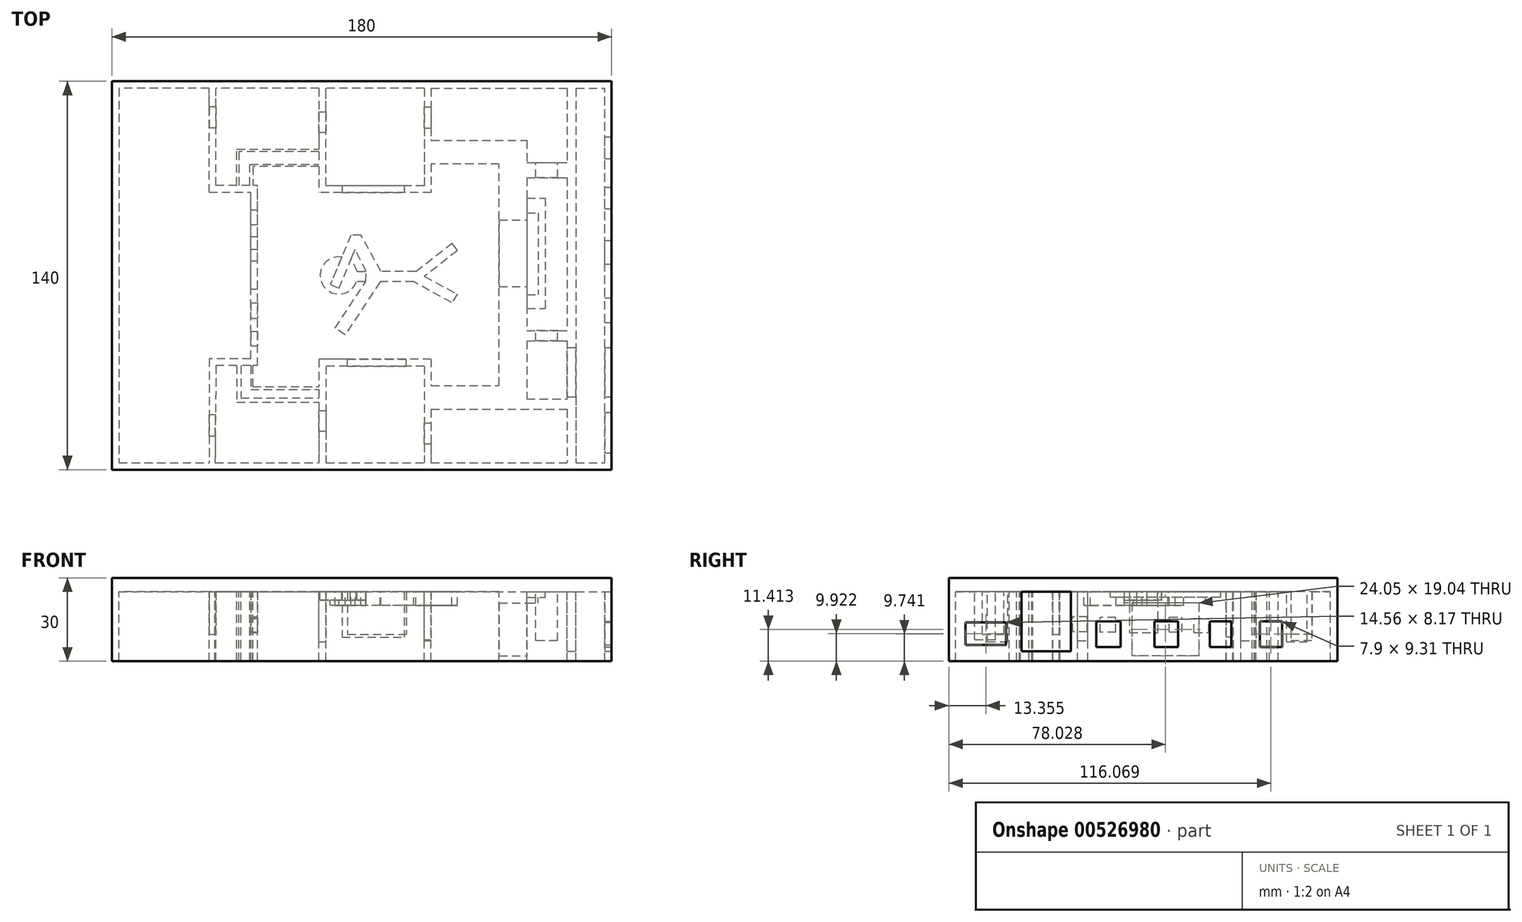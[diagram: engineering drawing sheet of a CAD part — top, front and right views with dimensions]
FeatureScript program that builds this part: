
annotation { "Feature Type Name" : "Feature", "Feature Type Description" : "" }
export const myFeature = defineFeature(function(context is Context, id is Id, definition is map)
    precondition{}
    {
        {
            var Q0;
            Q0=qCreatedBy(makeId("Top.planeOp"),FACE);
            var sketch = newSketch(context, id + "F0", { "sketchPlane" : qUnion([Q0])});
            skLineSegment(sketch, "E0", {"start": v(0, 0) * mm, "end": v(0, 140) * mm});
            skLineSegment(sketch, "E1", {"start": v(0, 140) * mm, "end": v(180, 140) * mm});
            skLineSegment(sketch, "E2", {"start": v(180, 140) * mm, "end": v(180, 0) * mm});
            skLineSegment(sketch, "E3", {"start": v(180, 0) * mm, "end": v(0, 0) * mm});
            skLineSegment(sketch, "E4", {"start": v(0, 140) * mm, "end": v(0, 136) * mm, "construction": true});
            skLineSegment(sketch, "E5", {"start": v(0, 140) * mm, "end": v(4, 140) * mm, "construction": true});
            skLineSegment(sketch, "E6", {"start": v(4, 136) * mm, "end": v(4, 0) * mm});
            skLineSegment(sketch, "E7", {"start": v(4, 136) * mm, "end": v(180, 136) * mm});
            skLineSegment(sketch, "E8", {"start": v(65.64, 100) * mm, "end": v(125.64, 100) * mm});
            skLineSegment(sketch, "E9", {"start": v(125.64, 100) * mm, "end": v(125.64, 40) * mm});
            skLineSegment(sketch, "E10", {"start": v(125.64, 40) * mm, "end": v(65.64, 40) * mm});
            skLineSegment(sketch, "E11", {"start": v(65.64, 100) * mm, "end": v(65.64, 40) * mm});
            skCircle(sketch, "E12", {"center": v(81.7, 70) * mm, "radius": 6.72 * mm});
            skPoint(sketch, "E12.centerSnap0", {"position": v(65.64, 70) * mm});
            skLineSegment(sketch, "E13", {"start": v(81.75, 65.36) * mm, "end": v(78.62, 66.66) * mm});
            skLineSegment(sketch, "E14", {"start": v(109.48, 71.46) * mm, "end": v(122.4, 81.58) * mm});
            skLineSegment(sketch, "E15", {"start": v(122.4, 81.58) * mm, "end": v(124.45, 78.96) * mm});
            skLineSegment(sketch, "E16", {"start": v(124.45, 78.96) * mm, "end": v(112.55, 69.63) * mm});
            skLineSegment(sketch, "E17", {"start": v(112.55, 69.63) * mm, "end": v(124.43, 63.28) * mm});
            skLineSegment(sketch, "E18", {"start": v(124.43, 63.28) * mm, "end": v(122.4, 60.22) * mm});
            skLineSegment(sketch, "E19", {"start": v(122.4, 60.22) * mm, "end": v(108.68, 67.74) * mm});
            skLineSegment(sketch, "E20", {"start": v(108.68, 67.74) * mm, "end": v(96.6, 67.74) * mm});
            skLineSegment(sketch, "E21", {"start": v(96.6, 67.74) * mm, "end": v(84, 48.65) * mm});
            skLineSegment(sketch, "E22", {"start": v(84, 48.65) * mm, "end": v(80.38, 51.04) * mm});
            skLineSegment(sketch, "E23", {"start": v(80.38, 51.04) * mm, "end": v(91.4, 67.74) * mm});
            skLineSegment(sketch, "E24", {"start": v(91.4, 67.74) * mm, "end": v(88.04, 67.74) * mm});
            skLineSegment(sketch, "E25", {"start": v(109.48, 71.46) * mm, "end": v(96.88, 71.46) * mm});
            skLineSegment(sketch, "E26", {"start": v(88.27, 71.46) * mm, "end": v(91.57, 71.46) * mm});
            skLineSegment(sketch, "E27", {"start": v(91.57, 71.46) * mm, "end": v(87.62, 79.42) * mm});
            skLineSegment(sketch, "E28", {"start": v(96.88, 71.46) * mm, "end": v(89.7, 84.59) * mm});
            skLineSegment(sketch, "E29", {"start": v(89.7, 84.59) * mm, "end": v(86.1, 84.59) * mm});
            skLineSegment(sketch, "E30", {"start": v(86.1, 84.59) * mm, "end": v(78.62, 66.66) * mm});
            skLineSegment(sketch, "E31", {"start": v(81.75, 65.36) * mm, "end": v(87.62, 79.42) * mm});
            skLineSegment(sketch, "E32", {"start": v(91.4, 67.74) * mm, "end": v(91.57, 71.46) * mm});
            skSolve(sketch);
        }
        {
            var Q0;
            Q0=makeQuery(id+"F0.imprint","IMPRINT",FACE,{"disambiguationData":[TD([[makeQuery(id+"F0.imprint","IMPRINT",EDGE,{"derivedFrom":sQuery(id+"F0.wireOp",EDGE,"E0")}),-1.0]])]});
            var Q1;
            {var subQ1=sQuery(id+"F0.wireOp",EDGE,"E6");Q1=makeQuery(id+"F0.imprint","IMPRINT",FACE,{"disambiguationData":[TD([[makeQuery(id+"F0.imprint","IMPRINT",EDGE,{"derivedFrom":subQ1}),1.0]])]});}
            var Q2;
            Q2=makeQuery(id+"F0.imprint","IMPRINT",FACE,{"disambiguationData":[TD([[makeQuery(id+"F0.imprint","IMPRINT",EDGE,{"derivedFrom":sQuery(id+"F0.wireOp",EDGE,"E8")}),-1.0]])]});
            var Q3;
            Q3=makeQuery(id+"F0.imprint","IMPRINT",FACE,{"disambiguationData":[TD([[makeQuery(id+"F0.imprint","IMPRINT",EDGE,{"derivedFrom":sQuery(id+"F0.wireOp",EDGE,"E14")}),-1.0]])]});
            var Q4;
            {var subQ0=sQuery(id+"F0.wireOp",EDGE,"E13");Q4=makeQuery(id+"F0.imprint","IMPRINT",FACE,{"disambiguationData":[TD([[makeQuery(id+"F0.imprint","IMPRINT",EDGE,{"derivedFrom":subQ0}),1.0]])]});}
            var Q5;
            {var subQ5=sQuery(id+"F0.wireOp",EDGE,"E13");Q5=makeQuery(id+"F0.imprint","IMPRINT",FACE,{"disambiguationData":[TD([[makeQuery(id+"F0.imprint","IMPRINT",EDGE,{"derivedFrom":subQ5}),-1.0]])]});}
            var Q6;
            {var subQ0=sQuery(id+"F0.wireOp",EDGE,"E26");Q6=makeQuery(id+"F0.imprint","IMPRINT",FACE,{"disambiguationData":[TD([[makeQuery(id+"F0.imprint","IMPRINT",EDGE,{"derivedFrom":subQ0}),1.0]])]});}
            var Q7;
            {var subQ0=sQuery(id+"F0.wireOp",EDGE,"E24");Q7=makeQuery(id+"F0.imprint","IMPRINT",FACE,{"disambiguationData":[TD([[makeQuery(id+"F0.imprint","IMPRINT",EDGE,{"derivedFrom":subQ0}),-1.0]])]});}
            extrude(context, id + "F1", {"entities" : qUnion([Q0, Q1, Q2, Q3, Q4, Q5, Q6, Q7]), "depth" : 5 * mm, "offsetDistance" : 25 * mm});
        }
        {
            var Q0;
            {var subQ0=sQuery(id+"F0.wireOp",EDGE,"E13");Q0=makeQuery(id+"F0.imprint","IMPRINT",FACE,{"disambiguationData":[TD([[makeQuery(id+"F0.imprint","IMPRINT",EDGE,{"derivedFrom":subQ0}),1.0]])]});}
            extrude(context, id + "F2", {"entities" : qUnion([Q0]), "oppositeDirection" : true, "depth" : 3 * mm, "offsetDistance" : 25 * mm});
        }
        {
            var Q0;
            Q0=makeQuery(id+"F0.imprint","IMPRINT",FACE,{"disambiguationData":[TD([[makeQuery(id+"F0.imprint","IMPRINT",EDGE,{"derivedFrom":sQuery(id+"F0.wireOp",EDGE,"E14")}),-1.0]])]});
            var Q1;
            {var subQ5=sQuery(id+"F0.wireOp",EDGE,"E13");Q1=makeQuery(id+"F0.imprint","IMPRINT",FACE,{"disambiguationData":[TD([[makeQuery(id+"F0.imprint","IMPRINT",EDGE,{"derivedFrom":subQ5}),-1.0]])]});}
            extrude(context, id + "F3", {"entities" : qUnion([Q0, Q1]), "oppositeDirection" : true, "depth" : 5 * mm, "offsetDistance" : 25 * mm});
        }
        {
            var Q0;
            {var subQ0=sQuery(id+"F0.wireOp",EDGE,"E24");Q0=makeQuery(id+"F0.imprint","IMPRINT",FACE,{"disambiguationData":[TD([[makeQuery(id+"F0.imprint","IMPRINT",EDGE,{"derivedFrom":subQ0}),-1.0]])]});}
            extrude(context, id + "F4", {"entities" : qUnion([Q0]), "operationType" : NewBodyOperationType.ADD, "oppositeDirection" : true, "depth" : 3 * mm, "offsetDistance" : 25 * mm});
        }
        {
            var Q0;
            {var subQ0=sQuery(id+"F0.wireOp",EDGE,"E0");var subQ1=sQuery(id+"F0.wireOp",EDGE,"E3");var subQ2=sQuery(id+"F0.wireOp",EDGE,"E1");var subQ3=sQuery(id+"F0.wireOp",EDGE,"E2");Q0=makeQuery(id+"F4.boolean.opBoolean","SPLIT",FACE,{"disambiguationData":[TD([makeQuery(id+"F1.opExtrude","SWEPT_FACE",FACE,{"disambiguationData":[OSD([subQ0])]})])],"derivedFrom":makeQuery(id+"F1.opExtrude","CAP_FACE",FACE,{"disambiguationData":[OSD([subQ0,subQ2,subQ3,subQ1])],"isStart":true})});}
            var sketch = newSketch(context, id + "F5", { "sketchPlane" : qUnion([Q0])});
            skLineSegment(sketch, "E33", {"start": v(0, -140) * mm, "end": v(0, -137.5) * mm, "construction": true});
            skLineSegment(sketch, "E34", {"start": v(0, -140) * mm, "end": v(2.5, -140) * mm, "construction": true});
            skLineSegment(sketch, "E35", {"start": v(180, -140) * mm, "end": v(180, -137.5) * mm, "construction": true});
            skLineSegment(sketch, "E36", {"start": v(180, -140) * mm, "end": v(177.5, -140) * mm, "construction": true});
            skLineSegment(sketch, "E37", {"start": v(180, 0) * mm, "end": v(177.5, 0) * mm, "construction": true});
            skLineSegment(sketch, "E38", {"start": v(180, 0) * mm, "end": v(180, -2.5) * mm, "construction": true});
            skLineSegment(sketch, "E39", {"start": v(177.5, 0) * mm, "end": v(180, 0) * mm});
            skLineSegment(sketch, "E40", {"start": v(180, -140) * mm, "end": v(0, -140) * mm});
            skLineSegment(sketch, "E41", {"start": v(0, 0) * mm, "end": v(180, 0) * mm});
            skLineSegment(sketch, "E42", {"start": v(65.99, -99.84) * mm, "end": v(65.7, -39.85) * mm, "construction": true});
            skLineSegment(sketch, "E43", {"start": v(2.5, -2.5) * mm, "end": v(52.5, -2.5) * mm, "construction": true});
            skLineSegment(sketch, "E44", {"start": v(2.5, -2.5) * mm, "end": v(2.5, -37.5) * mm, "construction": true});
            skLineSegment(sketch, "E45", {"start": v(2.5, -137.5) * mm, "end": v(2.5, -102.5) * mm, "construction": true});
            skLineSegment(sketch, "E46", {"start": v(52.5, -37.5) * mm, "end": v(52.5, -102.5) * mm});
            skLineSegment(sketch, "E47", {"start": v(2.5, -2.5) * mm, "end": v(37.13, -2.5) * mm, "construction": true});
            skLineSegment(sketch, "E48", {"start": v(37.5, -102.5) * mm, "end": v(37.5, -137.5) * mm});
            skLineSegment(sketch, "E49", {"start": v(37.5, -37.5) * mm, "end": v(37.13, -2.5) * mm});
            skLineSegment(sketch, "E50", {"start": v(37.5, -140) * mm, "end": v(35, -140) * mm, "construction": true});
            skLineSegment(sketch, "E51", {"start": v(52.5, -102.5) * mm, "end": v(52.5, -100) * mm, "construction": true});
            skLineSegment(sketch, "E52", {"start": v(35, -100) * mm, "end": v(35, -137.5) * mm});
            skLineSegment(sketch, "E53", {"start": v(52.5, -37.5) * mm, "end": v(50, -37.5) * mm, "construction": true});
            skLineSegment(sketch, "E54", {"start": v(35, -100) * mm, "end": v(50, -100) * mm});
            skLineSegment(sketch, "E55", {"start": v(52.5, -37.5) * mm, "end": v(52.5, -40) * mm, "construction": true});
            skLineSegment(sketch, "E56", {"start": v(37.5, -37.5) * mm, "end": v(35, -37.53) * mm, "construction": true});
            skLineSegment(sketch, "E57", {"start": v(50, -40) * mm, "end": v(35, -40) * mm});
            skLineSegment(sketch, "E58", {"start": v(35, -40) * mm, "end": v(35, -2.5) * mm});
            skLineSegment(sketch, "E59", {"start": v(50, -40) * mm, "end": v(50, -100) * mm});
            skLineSegment(sketch, "E60", {"start": v(112.49, -137.5) * mm, "end": v(114.99, -137.5) * mm, "construction": true});
            skLineSegment(sketch, "E61", {"start": v(114.99, -137.5) * mm, "end": v(114.99, -99.84) * mm});
            skLineSegment(sketch, "E62", {"start": v(114.99, -39.85) * mm, "end": v(114.99, -2.5) * mm});
            skLineSegment(sketch, "E63", {"start": v(74.59, -137.5) * mm, "end": v(77.09, -137.5) * mm, "construction": true});
            skLineSegment(sketch, "E64", {"start": v(114.99, -99.84) * mm, "end": v(114.99, -102.34) * mm, "construction": true});
            skLineSegment(sketch, "E65", {"start": v(112.49, -102.34) * mm, "end": v(77.09, -102.34) * mm});
            skLineSegment(sketch, "E66", {"start": v(77.09, -102.34) * mm, "end": v(77.09, -137.5) * mm});
            skLineSegment(sketch, "E67", {"start": v(112.49, -39.85) * mm, "end": v(112.49, -37.35) * mm, "construction": true});
            skLineSegment(sketch, "E68", {"start": v(112.49, -37.35) * mm, "end": v(77.09, -37.35) * mm});
            skLineSegment(sketch, "E69", {"start": v(112.49, -137.5) * mm, "end": v(77.09, -137.5) * mm});
            skLineSegment(sketch, "E70", {"start": v(74.59, -137.5) * mm, "end": v(37.5, -137.5) * mm});
            skLineSegment(sketch, "E71", {"start": v(35, -137.5) * mm, "end": v(2.5, -137.5) * mm});
            skLineSegment(sketch, "E72", {"start": v(2.5, -137.5) * mm, "end": v(2.5, -2.5) * mm});
            skLineSegment(sketch, "E73", {"start": v(2.5, -2.5) * mm, "end": v(35, -2.5) * mm});
            skLineSegment(sketch, "E74", {"start": v(37.13, -2.5) * mm, "end": v(74.59, -2.5) * mm});
            skLineSegment(sketch, "E75", {"start": v(77.09, -2.5) * mm, "end": v(112.49, -2.5) * mm});
            skLineSegment(sketch, "E76", {"start": v(114.99, -2.5) * mm, "end": v(177.5, -2.5) * mm});
            skLineSegment(sketch, "E77", {"start": v(177.5, -2.5) * mm, "end": v(177.5, -137.5) * mm});
            skLineSegment(sketch, "E78", {"start": v(112.49, -137.5) * mm, "end": v(112.49, -102.34) * mm});
            skLineSegment(sketch, "E79", {"start": v(114.99, -99.84) * mm, "end": v(74.59, -99.84) * mm});
            skLineSegment(sketch, "E80", {"start": v(112.49, -37.35) * mm, "end": v(112.49, -2.5) * mm});
            skLineSegment(sketch, "E81", {"start": v(114.99, -39.85) * mm, "end": v(74.59, -39.85) * mm});
            skLineSegment(sketch, "E82", {"start": v(77.09, -37.35) * mm, "end": v(77.09, -2.5) * mm});
            skLineSegment(sketch, "E83", {"start": v(114.99, -137.5) * mm, "end": v(177.5, -137.5) * mm});
            skLineSegment(sketch, "E84", {"start": v(180, 0) * mm, "end": v(0, 0) * mm});
            skLineSegment(sketch, "E85", {"start": v(0, 0) * mm, "end": v(0, -140) * mm});
            skLineSegment(sketch, "E86", {"start": v(0, -140) * mm, "end": v(180, -140) * mm});
            skLineSegment(sketch, "E87", {"start": v(180, -140) * mm, "end": v(180, 0) * mm});
            skLineSegment(sketch, "E88", {"start": v(49.7, -102.5) * mm, "end": v(49.7, -110.1) * mm});
            skLineSegment(sketch, "E89", {"start": v(49.7, -110.1) * mm, "end": v(74.59, -110.1) * mm});
            skLineSegment(sketch, "E90", {"start": v(74.59, -114.63) * mm, "end": v(45.73, -114.63) * mm});
            skLineSegment(sketch, "E91", {"start": v(45.73, -114.63) * mm, "end": v(45.73, -102.5) * mm});
            skLineSegment(sketch, "E92.bottom", {"start": v(50, -37.5) * mm, "end": v(50, -37.5) * mm});
            skLineSegment(sketch, "E92.top", {"start": v(50, -28.92) * mm, "end": v(50, -28.92) * mm});
            skLineSegment(sketch, "E92.left", {"start": v(50, -37.5) * mm, "end": v(50, -28.92) * mm});
            skLineSegment(sketch, "E92.right", {"start": v(50, -37.5) * mm, "end": v(50, -28.92) * mm});
            skLineSegment(sketch, "E93", {"start": v(50, -28.92) * mm, "end": v(74.59, -28.92) * mm});
            skLineSegment(sketch, "E94", {"start": v(46.44, -37.5) * mm, "end": v(46.44, -25.83) * mm});
            skLineSegment(sketch, "E95", {"start": v(46.44, -25.83) * mm, "end": v(74.59, -25.83) * mm});
            skLineSegment(sketch, "E96", {"start": v(45, -37.5) * mm, "end": v(45, -24.39) * mm});
            skLineSegment(sketch, "E97", {"start": v(45, -24.39) * mm, "end": v(74.59, -24.39) * mm});
            skLineSegment(sketch, "E98", {"start": v(74.59, -109.29) * mm, "end": v(50.75, -109.29) * mm});
            skLineSegment(sketch, "E99", {"start": v(50.75, -109.29) * mm, "end": v(50.75, -102.5) * mm});
            skLineSegment(sketch, "E100", {"start": v(45, -102.5) * mm, "end": v(45, -115.5) * mm});
            skLineSegment(sketch, "E101", {"start": v(45, -115.5) * mm, "end": v(74.59, -115.5) * mm});
            skLineSegment(sketch, "E102", {"start": v(50.68, -37.5) * mm, "end": v(50.68, -29.9) * mm});
            skLineSegment(sketch, "E103", {"start": v(50.68, -29.9) * mm, "end": v(74.59, -29.9) * mm});
            skLineSegment(sketch, "E104", {"start": v(114.99, -118.67) * mm, "end": v(149.45, -118.67) * mm});
            skLineSegment(sketch, "E105", {"start": v(149.45, -118.67) * mm, "end": v(149.45, -21.8) * mm});
            skLineSegment(sketch, "E106", {"start": v(149.45, -21.8) * mm, "end": v(114.99, -21.8) * mm});
            skLineSegment(sketch, "E107", {"start": v(163.9, -137.5) * mm, "end": v(163.9, -2.5) * mm});
            skLineSegment(sketch, "E108", {"start": v(167.19, -137.5) * mm, "end": v(167.19, -2.5) * mm});
            skLineSegment(sketch, "E109", {"start": v(52.5, -102.5) * mm, "end": v(50.75, -102.5) * mm});
            skLineSegment(sketch, "E110", {"start": v(49.7, -102.5) * mm, "end": v(45.73, -102.5) * mm});
            skLineSegment(sketch, "E111", {"start": v(45, -102.5) * mm, "end": v(37.5, -102.5) * mm});
            skLineSegment(sketch, "E112", {"start": v(74.59, -137.5) * mm, "end": v(74.59, -115.5) * mm});
            skLineSegment(sketch, "E113", {"start": v(74.59, -114.63) * mm, "end": v(74.59, -110.1) * mm});
            skLineSegment(sketch, "E114", {"start": v(74.59, -109.29) * mm, "end": v(74.59, -99.84) * mm});
            skLineSegment(sketch, "E115", {"start": v(74.59, -39.85) * mm, "end": v(74.59, -29.9) * mm});
            skLineSegment(sketch, "E116", {"start": v(74.59, -28.92) * mm, "end": v(74.59, -25.83) * mm});
            skLineSegment(sketch, "E117", {"start": v(74.59, -24.39) * mm, "end": v(74.59, -2.5) * mm});
            skLineSegment(sketch, "E118", {"start": v(52.5, -37.5) * mm, "end": v(50.68, -37.5) * mm});
            skLineSegment(sketch, "E119", {"start": v(50, -37.5) * mm, "end": v(46.44, -37.5) * mm});
            skLineSegment(sketch, "E120", {"start": v(45, -37.5) * mm, "end": v(37.5, -37.5) * mm});
            skLineSegment(sketch, "E121", {"start": v(149.45, -110.64) * mm, "end": v(163.9, -110.64) * mm});
            skLineSegment(sketch, "E122", {"start": v(149.45, -105.2) * mm, "end": v(163.9, -105.2) * mm});
            skLineSegment(sketch, "E123", {"start": v(149.45, -21.8) * mm, "end": v(163.9, -21.8) * mm});
            skLineSegment(sketch, "E124", {"start": v(149.45, -25.47) * mm, "end": v(163.9, -25.47) * mm});
            skLineSegment(sketch, "E125", {"start": v(149.45, -46.4) * mm, "end": v(163.9, -46.4) * mm});
            skLineSegment(sketch, "E126", {"start": v(149.45, -50.1) * mm, "end": v(163.9, -50.1) * mm});
            skLineSegment(sketch, "E127", {"start": v(163.9, -110.64) * mm, "end": v(163.9, -105.2) * mm});
            skLineSegment(sketch, "E128", {"start": v(149.45, -110.64) * mm, "end": v(149.45, -105.2) * mm});
            skLineSegment(sketch, "E129", {"start": v(149.45, -50.1) * mm, "end": v(149.45, -46.4) * mm});
            skLineSegment(sketch, "E130", {"start": v(163.9, -50.1) * mm, "end": v(163.9, -46.4) * mm});
            skLineSegment(sketch, "E131", {"start": v(149.45, -25.47) * mm, "end": v(149.45, -21.8) * mm});
            skLineSegment(sketch, "E132", {"start": v(163.9, -25.47) * mm, "end": v(163.9, -21.8) * mm});
            skLineSegment(sketch, "E133", {"start": v(163.9, -46.4) * mm, "end": v(163.9, -50.1) * mm});
            skLineSegment(sketch, "E134", {"start": v(114.99, -30.31) * mm, "end": v(139.5, -30.31) * mm});
            skLineSegment(sketch, "E135", {"start": v(139.5, -30.31) * mm, "end": v(139.5, -110.24) * mm});
            skLineSegment(sketch, "E136", {"start": v(139.5, -110.24) * mm, "end": v(114.99, -110.24) * mm});
            skSolve(sketch);
        }
        {
            var Q0;
            Q0=makeQuery(id+"F5.imprint","IMPRINT",FACE,{"disambiguationData":[TD([[makeQuery(id+"F5.imprint","IMPRINT",EDGE,{"derivedFrom":sQuery(id+"F5.wireOp",EDGE,"E46")}),-1.0]])]});
            var Q1;
            {var subQ0=sQuery(id+"F5.wireOp",EDGE,"E107");Q1=makeQuery(id+"F5.imprint","IMPRINT",FACE,{"disambiguationData":[TD([[makeQuery(id+"F5.imprint","IMPRINT",EDGE,{"derivedFrom":subQ0}),-1.0]])]});}
            var Q2;
            {var subQ1=sQuery(id+"F5.wireOp",EDGE,"zqTt42JP-UiR3-tYYN-FmIC-fksbVnWEhdpc");Q2=makeQuery(id+"F5.imprint","IMPRINT",FACE,{"disambiguationData":[TD([[makeQuery(id+"F5.imprint","IMPRINT",EDGE,{"derivedFrom":subQ1}),-1.0]])]});}
            var Q3;
            {var subQ4=sQuery(id+"F5.wireOp",EDGE,"BBN0Q2NJ-4y6p-QWxy-LSlA-rJ4cVUdJi9dW");Q3=makeQuery(id+"F5.imprint","IMPRINT",FACE,{"disambiguationData":[TD([[makeQuery(id+"F5.imprint","IMPRINT",EDGE,{"derivedFrom":subQ4}),-1.0]])]});}
            var Q4;
            {var subQ1=sQuery(id+"F5.wireOp",EDGE,"E94");Q4=makeQuery(id+"F5.imprint","IMPRINT",FACE,{"disambiguationData":[TD([[makeQuery(id+"F5.imprint","IMPRINT",EDGE,{"derivedFrom":subQ1}),1.0]])]});}
            var Q5;
            {var subQ3=sQuery(id+"F5.wireOp",EDGE,"E88");Q5=makeQuery(id+"F5.imprint","IMPRINT",FACE,{"disambiguationData":[TD([[makeQuery(id+"F5.imprint","IMPRINT",EDGE,{"derivedFrom":subQ3}),1.0]])]});}
            var Q6;
            Q6=sQuery(id+"F5.wireOp",EDGE,"E69");
            var Q7;
            Q7=sQuery(id+"F5.wireOp",EDGE,"E83");
            var Q8;
            Q8=sQuery(id+"F5.wireOp",EDGE,"E61");
            var Q9;
            Q9=sQuery(id+"F5.wireOp",EDGE,"E78");
            var Q10;
            Q10=sQuery(id+"F5.wireOp",EDGE,"E65");
            var Q11;
            Q11=sQuery(id+"F5.wireOp",EDGE,"E79");
            var Q12;
            Q12=sQuery(id+"F5.wireOp",EDGE,"E66");
            var Q13;
            Q13=sQuery(id+"F5.wireOp",EDGE,"xXiJbnCB-tXTr-yrwY-zz4e-hIO52vtba69x");
            var Q14;
            Q14=sQuery(id+"F5.wireOp",EDGE,"E70");
            var Q15;
            Q15=sQuery(id+"F5.wireOp",EDGE,"E48");
            var Q16;
            Q16=sQuery(id+"F5.wireOp",EDGE,"E52");
            var Q17;
            Q17=sQuery(id+"F5.wireOp",EDGE,"E72");
            var Q18;
            Q18=sQuery(id+"F0.wireOp",EDGE,"E6");
            var Q19;
            Q19=sQuery(id+"F5.wireOp",EDGE,"E71");
            var Q20;
            Q20=sQuery(id+"F5.wireOp",EDGE,"Ycx7GNkC-WWnf-lh6J-vGUQ-VtARFQnHF0Q5");
            var Q21;
            Q21=sQuery(id+"F5.wireOp",EDGE,"E54");
            var Q22;
            Q22=sQuery(id+"F5.wireOp",EDGE,"E46");
            var Q23;
            Q23=sQuery(id+"F5.wireOp",EDGE,"E59");
            var Q24;
            Q24=sQuery(id+"F5.wireOp",EDGE,"E57");
            var Q25;
            Q25=sQuery(id+"F5.wireOp",EDGE,"yTd8xMan-KKJn-cybX-pbuV-fECFdfSEL98J");
            var Q26;
            Q26=sQuery(id+"F5.wireOp",EDGE,"E49");
            var Q27;
            Q27=sQuery(id+"F5.wireOp",EDGE,"E58");
            var Q28;
            Q28=sQuery(id+"F5.wireOp",EDGE,"E73");
            var Q29;
            Q29=sQuery(id+"F5.wireOp",EDGE,"E84");
            var Q30;
            Q30=sQuery(id+"F5.wireOp",EDGE,"E74");
            var Q31;
            Q31=sQuery(id+"F5.wireOp",EDGE,"E81");
            var Q32;
            Q32=sQuery(id+"F5.wireOp",EDGE,"E62");
            var Q33;
            Q33=sQuery(id+"F5.wireOp",EDGE,"E80");
            var Q34;
            Q34=sQuery(id+"F5.wireOp",EDGE,"E82");
            var Q35;
            Q35=sQuery(id+"F5.wireOp",EDGE,"S9NegTVv-2bzC-NR3S-rT7V-91NvLfx18yFU");
            var Q36;
            Q36=sQuery(id+"F5.wireOp",EDGE,"E68");
            var Q37;
            Q37=sQuery(id+"F5.wireOp",EDGE,"E76");
            var Q38;
            Q38=sQuery(id+"F5.wireOp",EDGE,"E75");
            var Q39;
            Q39=sQuery(id+"F5.wireOp",EDGE,"E77");
            var Q40;
            Q40=sQuery(id+"F5.wireOp",EDGE,"E87");
            var Q41;
            Q41=sQuery(id+"F5.wireOp",EDGE,"E40");
            extrude(context, id + "F6", {"entities" : qUnion([Q0, Q1, Q2, Q3, Q4, Q5]), "surfaceEntities" : qUnion([Q6, Q7, Q8, Q9, Q10, Q11, Q12, Q13, Q14, Q15, Q16, Q17, Q18, Q19, Q20, Q21, Q22, Q23, Q24, Q25, Q26, Q27, Q28, Q29, Q30, Q31, Q32, Q33, Q34, Q35, Q36, Q37, Q38, Q39, Q40, Q41]), "depth" : 25 * mm, "offsetDistance" : 25 * mm});
        }
        {
            var Q0;
            Q0=makeQuery(id+"F6.opExtrude","SWEPT_FACE",FACE,{"disambiguationData":[OSD([sQuery(id+"F5.wireOp",EDGE,"E46")])]});
            var sketch = newSketch(context, id + "F7", { "sketchPlane" : qUnion([Q0])});
            skLineSegment(sketch, "E137", {"start": v(65.1, 0) * mm, "end": v(65.1, -14.76) * mm});
            skLineSegment(sketch, "E138", {"start": v(65.1, -14.76) * mm, "end": v(75.31, -14.76) * mm});
            skLineSegment(sketch, "E139", {"start": v(75.31, -14.76) * mm, "end": v(75.31, 0) * mm});
            skLineSegment(sketch, "E140", {"start": v(75.31, 0) * mm, "end": v(65.1, 0) * mm});
            skLineSegment(sketch, "E141.bottom", {"start": v(60.18, -14.58) * mm, "end": v(54.57, -14.58) * mm});
            skLineSegment(sketch, "E141.top", {"start": v(60.18, -9.25) * mm, "end": v(54.57, -9.25) * mm});
            skLineSegment(sketch, "E141.left", {"start": v(60.18, -14.58) * mm, "end": v(60.18, -9.25) * mm});
            skLineSegment(sketch, "E141.right", {"start": v(54.57, -14.58) * mm, "end": v(54.57, -9.25) * mm});
            skLineSegment(sketch, "E142.bottom", {"start": v(49.87, -14.43) * mm, "end": v(44.62, -14.43) * mm});
            skLineSegment(sketch, "E142.top", {"start": v(49.87, -9.05) * mm, "end": v(44.62, -9.05) * mm});
            skLineSegment(sketch, "E142.left", {"start": v(49.87, -14.43) * mm, "end": v(49.87, -9.05) * mm});
            skLineSegment(sketch, "E142.right", {"start": v(44.62, -14.43) * mm, "end": v(44.62, -9.05) * mm});
            skLineSegment(sketch, "E143.bottom", {"start": v(79.43, -14.5) * mm, "end": v(84.02, -14.5) * mm});
            skLineSegment(sketch, "E143.top", {"start": v(79.43, -9.1) * mm, "end": v(84.02, -9.1) * mm});
            skLineSegment(sketch, "E143.left", {"start": v(79.43, -14.5) * mm, "end": v(79.43, -9.1) * mm});
            skLineSegment(sketch, "E143.right", {"start": v(84.02, -14.5) * mm, "end": v(84.02, -9.1) * mm});
            skLineSegment(sketch, "E144.bottom", {"start": v(88.3, -14.67) * mm, "end": v(93.67, -14.67) * mm});
            skLineSegment(sketch, "E144.top", {"start": v(88.3, -9.6) * mm, "end": v(93.67, -9.6) * mm});
            skLineSegment(sketch, "E144.left", {"start": v(88.3, -14.67) * mm, "end": v(88.3, -9.6) * mm});
            skLineSegment(sketch, "E144.right", {"start": v(93.67, -14.67) * mm, "end": v(93.67, -9.6) * mm});
            skSolve(sketch);
        }
        {
            var Q0;
            Q0 = qSketchRegion(id + "F7", true);
            extrude(context, id + "F8", {"entities" : qUnion([Q0]), "operationType" : NewBodyOperationType.REMOVE, "oppositeDirection" : true, "depth" : 5 * mm, "offsetDistance" : 25 * mm});
        }
        {
            var Q0;
            Q0=makeQuery(id+"F5.imprint","IMPRINT",FACE,{"disambiguationData":[TD([[makeQuery(id+"F5.imprint","IMPRINT",EDGE,{"derivedFrom":sQuery(id+"F5.wireOp",EDGE,"E124")}),1.0]])]});
            var Q1;
            Q1=makeQuery(id+"F5.imprint","IMPRINT",FACE,{"disambiguationData":[TD([[makeQuery(id+"F5.imprint","IMPRINT",EDGE,{"derivedFrom":sQuery(id+"F5.wireOp",EDGE,"E126")}),1.0]])]});
            var Q2;
            Q2=makeQuery(id+"F5.imprint","IMPRINT",FACE,{"disambiguationData":[TD([[makeQuery(id+"F5.imprint","IMPRINT",EDGE,{"derivedFrom":sQuery(id+"F5.wireOp",EDGE,"E121")}),1.0]])]});
            extrude(context, id + "F9", {"entities" : qUnion([Q0, Q1, Q2]), "depth" : 25 * mm, "offsetDistance" : 25 * mm});
        }
        {
            var Q0;
            Q0=makeQuery(id+"F6.opExtrude","SWEPT_FACE",FACE,{"disambiguationData":[OSD([sQuery(id+"F5.wireOp",EDGE,"E48")])]});
            var sketch = newSketch(context, id + "F10", { "sketchPlane" : qUnion([Q0])});
            skLineSegment(sketch, "E145.bottom", {"start": v(130.84, 0) * mm, "end": v(123.2, 0) * mm});
            skLineSegment(sketch, "E145.top", {"start": v(130.84, -15.32) * mm, "end": v(123.2, -15.32) * mm});
            skLineSegment(sketch, "E145.left", {"start": v(130.84, 0) * mm, "end": v(130.84, -15.32) * mm});
            skLineSegment(sketch, "E145.right", {"start": v(123.2, 0) * mm, "end": v(123.2, -15.32) * mm});
            skLineSegment(sketch, "E146.bottom", {"start": v(19.83, 0) * mm, "end": v(12.17, 0) * mm});
            skLineSegment(sketch, "E146.top", {"start": v(19.83, -15.32) * mm, "end": v(12.17, -15.32) * mm});
            skLineSegment(sketch, "E146.left", {"start": v(19.83, 0) * mm, "end": v(19.83, -15.32) * mm});
            skLineSegment(sketch, "E146.right", {"start": v(12.17, 0) * mm, "end": v(12.17, -15.32) * mm});
            skSolve(sketch);
        }
        {
            var Q0;
            Q0=makeQuery(id+"F10.imprint","IMPRINT",FACE,{"disambiguationData":[TD([[makeQuery(id+"F10.imprint","IMPRINT",EDGE,{"derivedFrom":sQuery(id+"F10.wireOp",EDGE,"E145.bottom")}),-1.0]])]});
            var Q1;
            Q1=makeQuery(id+"F10.imprint","IMPRINT",FACE,{"disambiguationData":[TD([[makeQuery(id+"F10.imprint","IMPRINT",EDGE,{"derivedFrom":sQuery(id+"F10.wireOp",EDGE,"E146.bottom")}),1.0]])]});
            extrude(context, id + "F11", {"entities" : qUnion([Q0, Q1]), "operationType" : NewBodyOperationType.REMOVE, "oppositeDirection" : true, "depth" : 5 * mm, "offsetDistance" : 25 * mm});
        }
        {
            var Q0;
            Q0=makeQuery(id+"F6.opExtrude","SWEPT_FACE",FACE,{"disambiguationData":[OSD([sQuery(id+"F5.wireOp",EDGE,"E66")])]});
            var sketch = newSketch(context, id + "F12", { "sketchPlane" : qUnion([Q0])});
            skLineSegment(sketch, "E147.bottom", {"start": v(129.04, 0) * mm, "end": v(121.68, 0) * mm});
            skLineSegment(sketch, "E147.top", {"start": v(129.04, -17.99) * mm, "end": v(121.68, -17.99) * mm});
            skLineSegment(sketch, "E147.left", {"start": v(129.04, 0) * mm, "end": v(129.04, -17.99) * mm});
            skLineSegment(sketch, "E147.right", {"start": v(121.68, 0) * mm, "end": v(121.68, -17.99) * mm});
            skLineSegment(sketch, "E148.bottom", {"start": v(21.22, 0) * mm, "end": v(13.87, 0) * mm});
            skLineSegment(sketch, "E148.top", {"start": v(21.22, -17.99) * mm, "end": v(13.87, -17.99) * mm});
            skLineSegment(sketch, "E148.left", {"start": v(21.22, 0) * mm, "end": v(21.22, -17.99) * mm});
            skLineSegment(sketch, "E148.right", {"start": v(13.87, 0) * mm, "end": v(13.87, -17.99) * mm});
            skSolve(sketch);
        }
        {
            var Q0;
            Q0=makeQuery(id+"F12.imprint","IMPRINT",FACE,{"disambiguationData":[TD([[makeQuery(id+"F12.imprint","IMPRINT",EDGE,{"derivedFrom":sQuery(id+"F12.wireOp",EDGE,"E148.bottom")}),1.0]])]});
            var Q1;
            Q1=makeQuery(id+"F12.imprint","IMPRINT",FACE,{"disambiguationData":[TD([[makeQuery(id+"F12.imprint","IMPRINT",EDGE,{"derivedFrom":sQuery(id+"F12.wireOp",EDGE,"E147.bottom")}),-1.0]])]});
            extrude(context, id + "F13", {"entities" : qUnion([Q0, Q1]), "operationType" : NewBodyOperationType.REMOVE, "oppositeDirection" : true, "depth" : 25 * mm, "offsetDistance" : 25 * mm});
        }
        {
            var Q0;
            {var subQ0=sQuery(id+"F5.wireOp",EDGE,"E61");Q0=makeQuery(id+"F6.opExtrude","SWEPT_FACE",FACE,{"disambiguationData":[OSD([subQ0]),TDD([makeQuery(id+"F5.imprint","IMPRINT",EDGE,{"disambiguationData":[TD([[makeQuery(id+"F5.imprint","INTERSECT",VERTEX,{"derivedFrom":[subQ0,sQuery(id+"F5.wireOp",EDGE,"E83")]}),-1.0]])],"derivedFrom":subQ0})])]});}
            var sketch = newSketch(context, id + "F14", { "sketchPlane" : qUnion([Q0])});
            skLineSegment(sketch, "E149.bottom", {"start": v(130.76, 0) * mm, "end": v(123.19, 0) * mm});
            skLineSegment(sketch, "E149.top", {"start": v(130.76, -17.68) * mm, "end": v(123.19, -17.68) * mm});
            skLineSegment(sketch, "E149.left", {"start": v(130.76, 0) * mm, "end": v(130.76, -17.68) * mm});
            skLineSegment(sketch, "E149.right", {"start": v(123.19, 0) * mm, "end": v(123.19, -17.68) * mm});
            skLineSegment(sketch, "E150.bottom", {"start": v(16.86, 0) * mm, "end": v(9.36, 0) * mm});
            skLineSegment(sketch, "E150.top", {"start": v(16.86, -17.29) * mm, "end": v(9.36, -17.29) * mm});
            skLineSegment(sketch, "E150.left", {"start": v(16.86, 0) * mm, "end": v(16.86, -17.29) * mm});
            skLineSegment(sketch, "E150.right", {"start": v(9.36, 0) * mm, "end": v(9.36, -17.29) * mm});
            skSolve(sketch);
        }
        {
            var Q0;
            Q0=makeQuery(id+"F14.imprint","IMPRINT",FACE,{"disambiguationData":[TD([[makeQuery(id+"F14.imprint","IMPRINT",EDGE,{"derivedFrom":sQuery(id+"F14.wireOp",EDGE,"E149.bottom")}),1.0]])]});
            var Q1;
            Q1=makeQuery(id+"F14.imprint","IMPRINT",FACE,{"disambiguationData":[TD([[makeQuery(id+"F14.imprint","IMPRINT",EDGE,{"derivedFrom":sQuery(id+"F14.wireOp",EDGE,"E150.bottom")}),1.0]])]});
            extrude(context, id + "F15", {"entities" : qUnion([Q0, Q1]), "operationType" : NewBodyOperationType.REMOVE, "oppositeDirection" : true, "depth" : 25 * mm, "offsetDistance" : 25 * mm});
        }
        {
            var Q0;
            Q0=makeQuery(id+"F9.opExtrude","SWEPT_FACE",FACE,{"disambiguationData":[OSD([sQuery(id+"F5.wireOp",EDGE,"E121")])]});
            var sketch = newSketch(context, id + "F16", { "sketchPlane" : qUnion([Q0])});
            skLineSegment(sketch, "E151.bottom", {"start": v(-152.63, 0) * mm, "end": v(-160.53, 0) * mm});
            skLineSegment(sketch, "E151.top", {"start": v(-152.63, -17.69) * mm, "end": v(-160.53, -17.69) * mm});
            skLineSegment(sketch, "E151.left", {"start": v(-152.63, 0) * mm, "end": v(-152.63, -17.69) * mm});
            skLineSegment(sketch, "E151.right", {"start": v(-160.53, 0) * mm, "end": v(-160.53, -17.69) * mm});
            skSolve(sketch);
        }
        {
            var Q0;
            Q0=makeQuery(id+"F16.imprint","IMPRINT",FACE,{"disambiguationData":[TD([[makeQuery(id+"F16.imprint","IMPRINT",EDGE,{"derivedFrom":sQuery(id+"F16.wireOp",EDGE,"E151.bottom")}),1.0]])]});
            extrude(context, id + "F17", {"entities" : qUnion([Q0]), "operationType" : NewBodyOperationType.REMOVE, "oppositeDirection" : true, "depth" : 70 * mm, "offsetDistance" : 25 * mm});
        }
        {
            var Q0;
            Q0=makeQuery(id+"F6.opExtrude","SWEPT_FACE",FACE,{"disambiguationData":[OSD([sQuery(id+"F5.wireOp",EDGE,"E87")])]});
            var sketch = newSketch(context, id + "F18", { "sketchPlane" : qUnion([Q0])});
            skLineSegment(sketch, "E152.bottom", {"start": v(41.46, 0) * mm, "end": v(30.77, 0) * mm});
            skLineSegment(sketch, "E153.bottom", {"start": v(53.1, -19.91) * mm, "end": v(61.89, -19.91) * mm});
            skLineSegment(sketch, "E153.top", {"start": v(53.1, -10.65) * mm, "end": v(61.89, -10.65) * mm});
            skLineSegment(sketch, "E153.left", {"start": v(53.1, -19.91) * mm, "end": v(53.1, -10.65) * mm});
            skLineSegment(sketch, "E153.right", {"start": v(61.89, -19.91) * mm, "end": v(61.89, -10.65) * mm});
            skLineSegment(sketch, "E154.bottom", {"start": v(74.16, -19.91) * mm, "end": v(82.58, -19.91) * mm});
            skLineSegment(sketch, "E154.top", {"start": v(74.16, -10.63) * mm, "end": v(82.58, -10.63) * mm});
            skLineSegment(sketch, "E154.left", {"start": v(74.16, -19.91) * mm, "end": v(74.16, -10.63) * mm});
            skLineSegment(sketch, "E154.right", {"start": v(82.58, -19.91) * mm, "end": v(82.58, -10.63) * mm});
            skLineSegment(sketch, "E155.bottom", {"start": v(94.07, -19.91) * mm, "end": v(101.75, -19.91) * mm});
            skLineSegment(sketch, "E155.top", {"start": v(94.07, -10.64) * mm, "end": v(101.75, -10.64) * mm});
            skLineSegment(sketch, "E155.left", {"start": v(94.07, -19.91) * mm, "end": v(94.07, -10.64) * mm});
            skLineSegment(sketch, "E155.right", {"start": v(101.75, -19.91) * mm, "end": v(101.75, -10.64) * mm});
            skLineSegment(sketch, "E156.bottom", {"start": v(112.12, -19.91) * mm, "end": v(120.02, -19.91) * mm});
            skLineSegment(sketch, "E156.top", {"start": v(112.12, -10.6) * mm, "end": v(120.02, -10.6) * mm});
            skLineSegment(sketch, "E156.left", {"start": v(112.12, -19.91) * mm, "end": v(112.12, -10.6) * mm});
            skLineSegment(sketch, "E156.right", {"start": v(120.02, -19.91) * mm, "end": v(120.02, -10.6) * mm});
            skLineSegment(sketch, "E157.bottom", {"start": v(20.64, -19.16) * mm, "end": v(6.07, -19.16) * mm});
            skLineSegment(sketch, "E157.top", {"start": v(20.64, -11) * mm, "end": v(6.07, -11) * mm});
            skLineSegment(sketch, "E157.left", {"start": v(20.64, -19.16) * mm, "end": v(20.64, -11) * mm});
            skLineSegment(sketch, "E157.right", {"start": v(6.07, -19.16) * mm, "end": v(6.07, -11) * mm});
            skLineSegment(sketch, "E158.bottom", {"start": v(44.03, 0) * mm, "end": v(26.22, 0) * mm});
            skLineSegment(sketch, "E158.top", {"start": v(44.03, -21.5) * mm, "end": v(26.22, -21.5) * mm});
            skLineSegment(sketch, "E158.left", {"start": v(44.03, 0) * mm, "end": v(44.03, -21.5) * mm});
            skLineSegment(sketch, "E158.right", {"start": v(26.22, 0) * mm, "end": v(26.22, -21.5) * mm});
            skSolve(sketch);
        }
        {
            var Q0;
            Q0=makeQuery(id+"F18.imprint","IMPRINT",FACE,{"disambiguationData":[TD([[makeQuery(id+"F18.imprint","IMPRINT",EDGE,{"derivedFrom":sQuery(id+"F18.wireOp",EDGE,"E155.bottom")}),1.0]])]});
            var Q1;
            Q1=makeQuery(id+"F18.imprint","IMPRINT",FACE,{"disambiguationData":[TD([[makeQuery(id+"F18.imprint","IMPRINT",EDGE,{"derivedFrom":sQuery(id+"F18.wireOp",EDGE,"E154.bottom")}),1.0]])]});
            var Q2;
            Q2=makeQuery(id+"F18.imprint","IMPRINT",FACE,{"disambiguationData":[TD([[makeQuery(id+"F18.imprint","IMPRINT",EDGE,{"derivedFrom":sQuery(id+"F18.wireOp",EDGE,"E156.bottom")}),1.0]])]});
            var Q3;
            Q3=makeQuery(id+"F18.imprint","IMPRINT",FACE,{"disambiguationData":[TD([[makeQuery(id+"F18.imprint","IMPRINT",EDGE,{"derivedFrom":sQuery(id+"F18.wireOp",EDGE,"E153.bottom")}),1.0]])]});
            var Q4;
            Q4=makeQuery(id+"F18.imprint","IMPRINT",FACE,{"disambiguationData":[TD([[makeQuery(id+"F18.imprint","IMPRINT",EDGE,{"derivedFrom":sQuery(id+"F18.wireOp",EDGE,"E157.bottom")}),-1.0]])]});
            extrude(context, id + "F19", {"entities" : qUnion([Q0, Q1, Q2, Q3, Q4]), "operationType" : NewBodyOperationType.REMOVE, "oppositeDirection" : true, "depth" : 5 * mm, "offsetDistance" : 25 * mm});
        }
        {
            var Q0;
            {var subQ7=sQuery(id+"F5.wireOp",EDGE,"E104");Q0=makeQuery(id+"F5.imprint","IMPRINT",FACE,{"disambiguationData":[TD([[makeQuery(id+"F5.imprint","IMPRINT",EDGE,{"derivedFrom":subQ7}),1.0]])]});}
            extrude(context, id + "F20", {"entities" : qUnion([Q0]), "operationType" : NewBodyOperationType.ADD, "depth" : 25 * mm, "offsetDistance" : 25 * mm});
        }
        {
            var Q0;
            Q0=makeQuery(id+"F18.imprint","IMPRINT",FACE,{"disambiguationData":[TD([[makeQuery(id+"F18.imprint","IMPRINT",EDGE,{"derivedFrom":sQuery(id+"F18.wireOp",EDGE,"E158.top")}),-1.0]])]});
            extrude(context, id + "F21", {"entities" : qUnion([Q0]), "operationType" : NewBodyOperationType.REMOVE, "oppositeDirection" : true, "depth" : 25 * mm, "offsetDistance" : 25 * mm});
        }
        {
            var Q0;
            {var subQ1=sQuery(id+"F0.wireOp",EDGE,"E6");Q0=makeQuery(id+"F0.imprint","IMPRINT",FACE,{"disambiguationData":[TD([[makeQuery(id+"F0.imprint","IMPRINT",EDGE,{"derivedFrom":subQ1}),1.0]])]});}
            var sketch = newSketch(context, id + "F22", { "sketchPlane" : qUnion([Q0])});
            skLineSegment(sketch, "E159.bottom", {"start": v(149.5, 97.91) * mm, "end": v(156.11, 97.91) * mm});
            skLineSegment(sketch, "E159.top", {"start": v(149.5, 58.18) * mm, "end": v(156.11, 58.18) * mm});
            skLineSegment(sketch, "E159.left", {"start": v(149.5, 97.91) * mm, "end": v(149.5, 58.18) * mm});
            skLineSegment(sketch, "E159.right", {"start": v(156.11, 97.91) * mm, "end": v(156.11, 58.18) * mm});
            skLineSegment(sketch, "E160.bottom", {"start": v(149.5, 92.49) * mm, "end": v(153.5, 92.49) * mm});
            skLineSegment(sketch, "E160.top", {"start": v(149.5, 63.11) * mm, "end": v(153.5, 63.11) * mm});
            skLineSegment(sketch, "E160.left", {"start": v(149.5, 92.49) * mm, "end": v(149.5, 63.11) * mm});
            skLineSegment(sketch, "E160.right", {"start": v(153.5, 92.49) * mm, "end": v(153.5, 63.11) * mm});
            skSolve(sketch);
        }
        {
            var Q0;
            {var subQ4=sQuery(id+"F22.wireOp",EDGE,"E159.bottom");Q0=makeQuery(id+"F22.imprint","IMPRINT",FACE,{"disambiguationData":[TD([[makeQuery(id+"F22.imprint","IMPRINT",EDGE,{"derivedFrom":subQ4}),-1.0]])]});}
            extrude(context, id + "F23", {"entities" : qUnion([Q0]), "operationType" : NewBodyOperationType.ADD, "oppositeDirection" : true, "depth" : 2 * mm, "offsetDistance" : 25 * mm});
        }
        {
            var Q0;
            Q0=makeQuery(id+"F22.imprint","IMPRINT",FACE,{"disambiguationData":[TD([[makeQuery(id+"F22.imprint","IMPRINT",EDGE,{"derivedFrom":sQuery(id+"F22.wireOp",EDGE,"E160.bottom")}),-1.0]])]});
            extrude(context, id + "F24", {"entities" : qUnion([Q0]), "operationType" : NewBodyOperationType.ADD, "oppositeDirection" : true, "depth" : 4 * mm, "offsetDistance" : 25 * mm});
        }
        {
            var Q0;
            {var subQ0=sQuery(id+"F5.wireOp",EDGE,"E122");var subQ2=sQuery(id+"F5.wireOp",EDGE,"E131");var subQ3=sQuery(id+"F5.wireOp",EDGE,"E128");var subQ8=sQuery(id+"F5.wireOp",EDGE,"E129");var subQ10=sQuery(id+"F5.wireOp",EDGE,"E105");Q0=makeQuery(id+"F20.boolean.opBoolean","SPLIT",FACE,{"disambiguationData":[TD([makeQuery(id+"F9.opExtrude","SWEPT_FACE",FACE,{"disambiguationData":[OSD([subQ0])]})])],"derivedFrom":makeQuery(id+"F20.opExtrude","SWEPT_FACE",FACE,{"disambiguationData":[OSD([subQ10,subQ3,subQ8,subQ2])]})});}
            var sketch = newSketch(context, id + "F25", { "sketchPlane" : qUnion([Q0])});
            skLineSegment(sketch, "E161.bottom", {"start": v(90.05, -4.07) * mm, "end": v(66, -4.07) * mm});
            skLineSegment(sketch, "E161.top", {"start": v(90.05, -23.1) * mm, "end": v(66, -23.1) * mm});
            skLineSegment(sketch, "E161.left", {"start": v(90.05, -4.07) * mm, "end": v(90.05, -23.1) * mm});
            skLineSegment(sketch, "E161.right", {"start": v(66, -4.07) * mm, "end": v(66, -23.1) * mm});
            skSolve(sketch);
        }
        {
            var Q0;
            Q0=makeQuery(id+"F25.imprint","IMPRINT",FACE,{"disambiguationData":[TD([[makeQuery(id+"F25.imprint","IMPRINT",EDGE,{"derivedFrom":sQuery(id+"F25.wireOp",EDGE,"E161.bottom")}),1.0]])]});
            extrude(context, id + "F26", {"entities" : qUnion([Q0]), "operationType" : NewBodyOperationType.REMOVE, "oppositeDirection" : true, "depth" : 10 * mm, "offsetDistance" : 25 * mm});
        }
        {
            var Q0;
            Q0=makeQuery(id+"F6.opExtrude","SWEPT_FACE",FACE,{"disambiguationData":[OSD([sQuery(id+"F5.wireOp",EDGE,"E81")])]});
            var sketch = newSketch(context, id + "F27", { "sketchPlane" : qUnion([Q0])});
            skLineSegment(sketch, "E162.bottom", {"start": v(-84.85, 0) * mm, "end": v(-106.02, 0) * mm});
            skLineSegment(sketch, "E162.top", {"start": v(-84.85, -15.36) * mm, "end": v(-106.02, -15.36) * mm});
            skLineSegment(sketch, "E162.left", {"start": v(-84.85, 0) * mm, "end": v(-84.85, -15.36) * mm});
            skLineSegment(sketch, "E162.right", {"start": v(-106.02, 0) * mm, "end": v(-106.02, -15.36) * mm});
            skSolve(sketch);
        }
        {
            var Q0;
            Q0=makeQuery(id+"F27.imprint","IMPRINT",FACE,{"disambiguationData":[TD([[makeQuery(id+"F27.imprint","IMPRINT",EDGE,{"derivedFrom":sQuery(id+"F27.wireOp",EDGE,"E162.bottom")}),-1.0]])]});
            extrude(context, id + "F28", {"entities" : qUnion([Q0]), "operationType" : NewBodyOperationType.REMOVE, "oppositeDirection" : true, "depth" : 25 * mm, "offsetDistance" : 25 * mm});
        }
        {
            var Q0;
            Q0=makeQuery(id+"F6.opExtrude","SWEPT_FACE",FACE,{"disambiguationData":[OSD([sQuery(id+"F5.wireOp",EDGE,"E79")])]});
            var sketch = newSketch(context, id + "F29", { "sketchPlane" : qUnion([Q0])});
            skLineSegment(sketch, "E163.bottom", {"start": v(82.88, 0) * mm, "end": v(105.25, 0) * mm});
            skLineSegment(sketch, "E163.top", {"start": v(82.88, -16.32) * mm, "end": v(105.25, -16.32) * mm});
            skLineSegment(sketch, "E163.left", {"start": v(82.88, 0) * mm, "end": v(82.88, -16.32) * mm});
            skLineSegment(sketch, "E163.right", {"start": v(105.25, 0) * mm, "end": v(105.25, -16.32) * mm});
            skSolve(sketch);
        }
        {
            var Q0;
            Q0=makeQuery(id+"F29.imprint","IMPRINT",FACE,{"disambiguationData":[TD([[makeQuery(id+"F29.imprint","IMPRINT",EDGE,{"derivedFrom":sQuery(id+"F29.wireOp",EDGE,"E163.bottom")}),1.0]])]});
            extrude(context, id + "F30", {"entities" : qUnion([Q0]), "operationType" : NewBodyOperationType.REMOVE, "oppositeDirection" : true, "depth" : 25 * mm, "offsetDistance" : 25 * mm});
        }
    });
